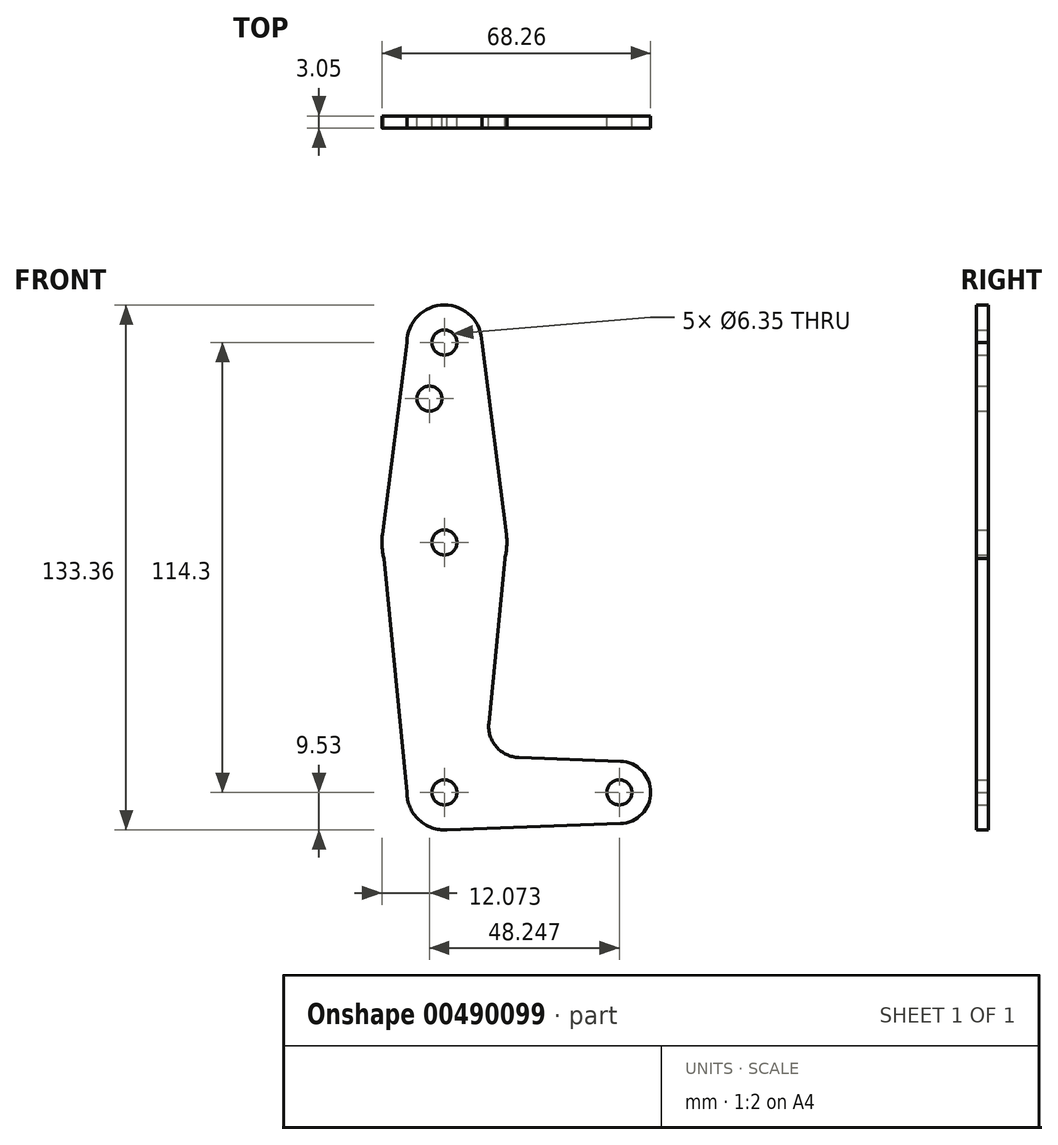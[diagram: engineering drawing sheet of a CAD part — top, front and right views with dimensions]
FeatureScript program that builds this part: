
annotation { "Feature Type Name" : "Feature", "Feature Type Description" : "" }
export const myFeature = defineFeature(function(context is Context, id is Id, definition is map)
    precondition{}
    {
        {
            var Q0;
            Q0=qCreatedBy(makeId("Front.planeOp"),FACE);
            var sketch = newSketch(context, id + "F0", { "sketchPlane" : qUnion([Q0])});
            skLineSegment(sketch, "E0", {"start": v(0, 114.3) * mm, "end": v(0, 0) * mm, "construction": true});
            skLineSegment(sketch, "E1", {"start": v(0, 0) * mm, "end": v(44.45, 0) * mm, "construction": true});
            skCircle(sketch, "E2", {"center": v(0, 114.3) * mm, "radius": 9.53 * mm});
            skCircle(sketch, "E3", {"center": v(0, 63.5) * mm, "radius": 15.88 * mm});
            skCircle(sketch, "E4", {"center": v(0, 0) * mm, "radius": 9.53 * mm});
            skCircle(sketch, "E5", {"center": v(44.45, 0) * mm, "radius": 7.94 * mm});
            skLineSegment(sketch, "E6", {"start": v(18.9, 8.85) * mm, "end": v(44.73, 7.93) * mm});
            skLineSegment(sketch, "E7", {"start": v(0, -9.53) * mm, "end": v(44.73, -7.93) * mm});
            skLineSegment(sketch, "E8", {"start": v(9.52, 114.3) * mm, "end": v(15.75, 65.5) * mm});
            skLineSegment(sketch, "E9", {"start": v(-9.53, 114.3) * mm, "end": v(-15.75, 65.5) * mm});
            skLineSegment(sketch, "E10", {"start": v(15.75, 63.5) * mm, "end": v(11.28, 17.57) * mm});
            skLineSegment(sketch, "E11", {"start": v(-9.52, 0) * mm, "end": v(-15.75, 63.5) * mm});
            skCircle(sketch, "E12", {"center": v(0, 114.3) * mm, "radius": 3.18 * mm});
            skCircle(sketch, "E13", {"center": v(0, 63.5) * mm, "radius": 3.18 * mm});
            skCircle(sketch, "E14", {"center": v(0, 0) * mm, "radius": 3.18 * mm});
            skCircle(sketch, "E15", {"center": v(44.45, 0) * mm, "radius": 3.18 * mm});
            skCircle(sketch, "E16", {"center": v(-3.8, 100.03) * mm, "radius": 3.18 * mm});
            skArc(sketch, "E17.filletArc", {"start": v(11.28, 17.57) * mm, "mid": v(13.21, 11.56) * mm, "end": v(18.9, 8.85) * mm});
            skSolve(sketch);
        }
        {
            var Q0;
            Q0 = qSketchRegion(id + "F0", true);
            extrude(context, id + "F1", {"entities" : qUnion([Q0]), "depth" : 3.05 * mm});
        }
    });
